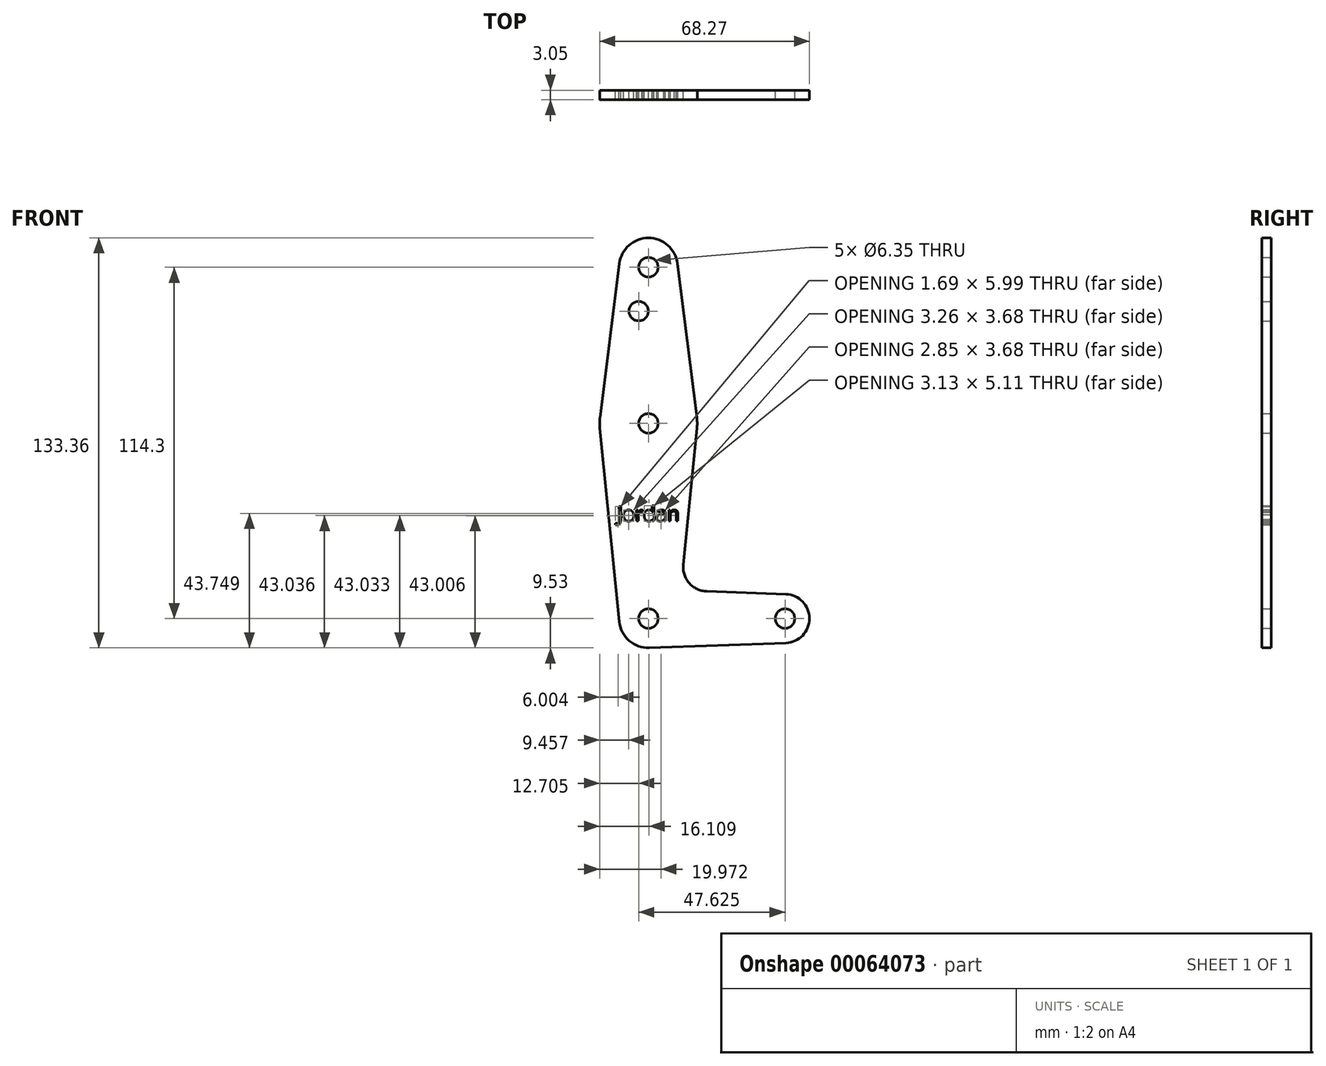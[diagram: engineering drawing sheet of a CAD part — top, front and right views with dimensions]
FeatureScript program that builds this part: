
annotation { "Feature Type Name" : "Feature", "Feature Type Description" : "" }
export const myFeature = defineFeature(function(context is Context, id is Id, definition is map)
    precondition{}
    {
        {
            var Q0;
            Q0=qCreatedBy(makeId("Front.planeOp"),FACE);
            var sketch = newSketch(context, id + "F0", { "sketchPlane" : qUnion([Q0])});
            skLineSegment(sketch, "E0", {"start": v(0, 0) * mm, "end": v(0, 63.5) * mm, "construction": true});
            skLineSegment(sketch, "E1", {"start": v(0, 63.5) * mm, "end": v(0, 114.3) * mm, "construction": true});
            skLineSegment(sketch, "E2", {"start": v(0, 0) * mm, "end": v(44.45, 0) * mm, "construction": true});
            skCircle(sketch, "E3", {"center": v(0, 114.3) * mm, "radius": 9.53 * mm});
            skCircle(sketch, "E4", {"center": v(0, 63.5) * mm, "radius": 15.88 * mm});
            skCircle(sketch, "E5", {"center": v(0, 0) * mm, "radius": 9.53 * mm});
            skCircle(sketch, "E6", {"center": v(44.45, 0) * mm, "radius": 7.94 * mm});
            skLineSegment(sketch, "E7", {"start": v(-9.45, 115.5) * mm, "end": v(-15.75, 65.48) * mm});
            skLineSegment(sketch, "E8", {"start": v(9.45, 115.5) * mm, "end": v(15.75, 65.48) * mm});
            skLineSegment(sketch, "E9", {"start": v(-15.8, 61.91) * mm, "end": v(-9.48, -0.95) * mm});
            skLineSegment(sketch, "E10", {"start": v(15.8, 61.91) * mm, "end": v(11.34, 17.6) * mm});
            skLineSegment(sketch, "E11", {"start": v(0.34, -9.52) * mm, "end": v(44.73, -7.93) * mm});
            skLineSegment(sketch, "E12", {"start": v(18.97, 8.85) * mm, "end": v(44.73, 7.93) * mm});
            skCircle(sketch, "E13", {"center": v(0, 114.3) * mm, "radius": 3.18 * mm});
            skCircle(sketch, "E14", {"center": v(-3.17, 100.03) * mm, "radius": 3.18 * mm});
            skCircle(sketch, "E15", {"center": v(0, 63.5) * mm, "radius": 3.18 * mm});
            skCircle(sketch, "E16", {"center": v(0, 0) * mm, "radius": 3.18 * mm});
            skCircle(sketch, "E17", {"center": v(44.45, 0) * mm, "radius": 3.18 * mm});
            skArc(sketch, "E18.filletArc", {"start": v(11.34, 17.6) * mm, "mid": v(13.26, 11.57) * mm, "end": v(18.97, 8.85) * mm});
            skLineSegment(sketch, "E19", {"start": v(-3.17, 100.03) * mm, "end": v(-3.17, 63.5) * mm, "construction": true});
            skLineSegment(sketch, "E20", {"start": v(-3.17, 92.24) * mm, "end": v(0, 92.24) * mm, "construction": true});
            skText(sketch, "E21", { "text": "Jordan", "fontName": "OpenSans-Regular.ttf"});
            const initialGuessF0  = {"E21": [-0.0102, 0.03173, 1, 0, 0.00478]};
            skSetInitialGuess(sketch, initialGuessF0);
            skSolve(sketch);
        }
        {
            var Q0;
            Q0 = qSketchRegion(id + "F0", true);
            extrude(context, id + "F1", {"entities" : qUnion([Q0]), "depth" : 3.05 * mm});
        }
    });
